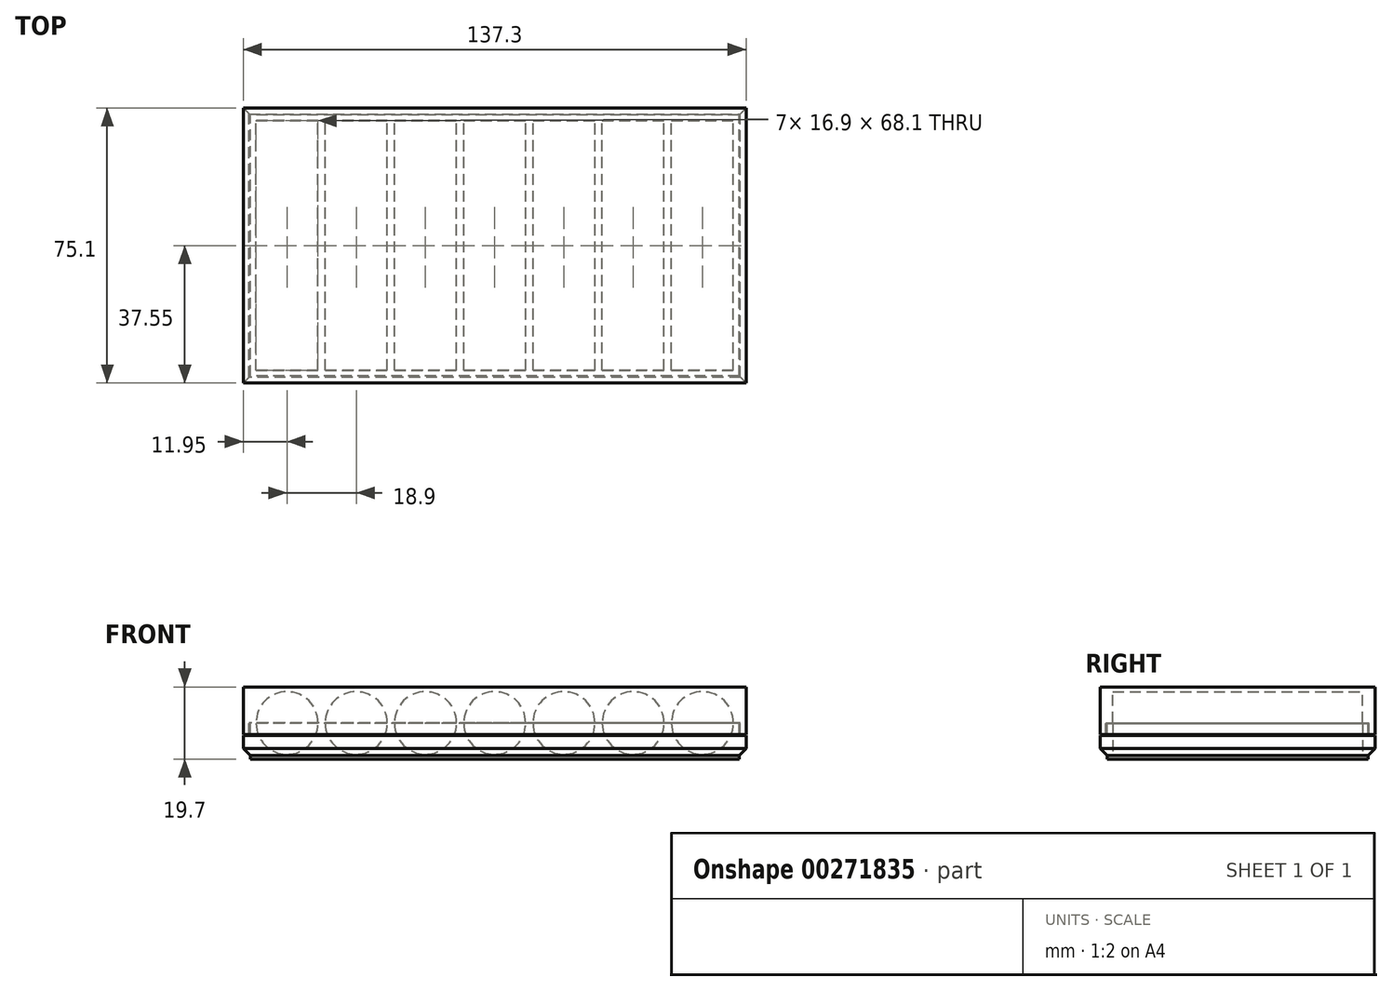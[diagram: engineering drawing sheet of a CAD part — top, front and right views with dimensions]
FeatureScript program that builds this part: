
annotation { "Feature Type Name" : "Feature", "Feature Type Description" : "" }
export const myFeature = defineFeature(function(context is Context, id is Id, definition is map)
    precondition{}
    {
        {
            assignVariable(context, id + "F0", {"name" : "chaff", "anyValue" : .3});
        }
        {
            assignVariable(context, id + "F1", {"name" : "basethick", "anyValue" : 1});
        }
        {
            assignVariable(context, id + "F2", {"name" : "diskdiam", "anyValue" : 16.3});
        }
        {
            assignVariable(context, id + "F3", {"name" : "lidrimdepth", "anyValue" : 3});
        }
        {
            var Q0;
            Q0=qCreatedBy(makeId("Top.planeOp"),FACE);
            var sketch = newSketch(context, id + "F4", { "sketchPlane" : qUnion([Q0])});
            skLineSegment(sketch, "E0.bottom", {"start": v(68.65, -37.55) * mm, "end": v(-68.65, -37.55) * mm});
            skLineSegment(sketch, "E0.top", {"start": v(68.65, 37.55) * mm, "end": v(-68.65, 37.55) * mm});
            skLineSegment(sketch, "E0.left", {"start": v(68.65, -37.55) * mm, "end": v(68.65, 37.55) * mm});
            skLineSegment(sketch, "E0.right", {"start": v(-68.65, -37.55) * mm, "end": v(-68.65, 37.55) * mm});
            skPoint(sketch, "E0.middle", {"position": v(0, 0) * mm});
            skSolve(sketch);
        }
        {
            var Q0;
            Q0=qSketchRegion(id+"F4",true);
            extrude(context, id + "F5", {"entities" : qUnion([Q0]), "depth" : (getVariable(context, 'basethick')) * mm});
        }
        {
            var Q0;
            Q0=makeQuery(id+"F5.opExtrude","CAP_FACE",FACE,{"disambiguationData":[OSD([sQuery(id+"F4.wireOp",EDGE,"E0.bottom"),sQuery(id+"F4.wireOp",EDGE,"E0.top"),sQuery(id+"F4.wireOp",EDGE,"E0.left"),sQuery(id+"F4.wireOp",EDGE,"E0.right")])],"isStart":false});
            var sketch = newSketch(context, id + "F6", { "sketchPlane" : qUnion([Q0])});
            skLineSegment(sketch, "E1.bottom", {"start": v(65.15, -34.05) * mm, "end": v(-65.15, -34.05) * mm});
            skLineSegment(sketch, "E1.top", {"start": v(65.15, 34.05) * mm, "end": v(-65.15, 34.05) * mm});
            skLineSegment(sketch, "E1.left", {"start": v(65.15, -34.05) * mm, "end": v(65.15, 34.05) * mm});
            skLineSegment(sketch, "E1.right", {"start": v(-65.15, -34.05) * mm, "end": v(-65.15, 34.05) * mm});
            skPoint(sketch, "E1.middle", {"position": v(0, 0) * mm});
            skLineSegment(sketch, "E2", {"start": v(-68.65, 0) * mm, "end": v(-65.15, 0) * mm, "construction": true});
            skLineSegment(sketch, "E3", {"start": v(0, 34.05) * mm, "end": v(0, 37.55) * mm, "construction": true});
            skLineSegment(sketch, "E4.0", {"start": v(-68.65, -37.55) * mm, "end": v(-68.65, 37.55) * mm});
            skLineSegment(sketch, "E5.0", {"start": v(68.65, -37.55) * mm, "end": v(-68.65, -37.55) * mm});
            skLineSegment(sketch, "E6.0", {"start": v(68.65, -37.55) * mm, "end": v(68.65, 37.55) * mm});
            skLineSegment(sketch, "E7.0", {"start": v(68.65, 37.55) * mm, "end": v(-68.65, 37.55) * mm});
            skSolve(sketch);
        }
        {
            var Q0;
            Q0=qSketchRegion(id+"F6",true);
            extrude(context, id + "F7", {"entities" : qUnion([Q0]), "operationType" : NewBodyOperationType.ADD, "depth" : (getVariable(context, 'diskdiam') / 2 + getVariable(context, 'chaff') * 2) * mm});
        }
        {
            var Q0;
            Q0=makeQuery(id+"F7.opExtrude","SWEPT_FACE",FACE,{"disambiguationData":[OSD([sQuery(id+"F6.wireOp",EDGE,"E1.top")])]});
            var sketch = newSketch(context, id + "F8", { "sketchPlane" : qUnion([Q0])});
            skLineSegment(sketch, "E8", {"start": v(-65.15, 9.75) * mm, "end": v(-48.25, 9.75) * mm});
            skArc(sketch, "E9", {"start": v(-65.15, 9.75) * mm, "mid": v(-56.7, 1.3) * mm, "end": v(-48.25, 9.75) * mm});
            skLineSegment(sketch, "E10.1.0.0", {"start": v(-46.25, 9.75) * mm, "end": v(-29.35, 9.75) * mm});
            skArc(sketch, "E10.1.0.1", {"start": v(-46.25, 9.75) * mm, "mid": v(-37.8, 1.3) * mm, "end": v(-29.35, 9.75) * mm});
            skLineSegment(sketch, "E10.2.0.0", {"start": v(-27.35, 9.75) * mm, "end": v(-10.45, 9.75) * mm});
            skArc(sketch, "E10.2.0.1", {"start": v(-27.35, 9.75) * mm, "mid": v(-18.9, 1.3) * mm, "end": v(-10.45, 9.75) * mm});
            skLineSegment(sketch, "E10.3.0.0", {"start": v(-8.45, 9.75) * mm, "end": v(8.45, 9.75) * mm});
            skArc(sketch, "E10.3.0.1", {"start": v(-8.45, 9.75) * mm, "mid": v(0, 1.3) * mm, "end": v(8.45, 9.75) * mm});
            skLineSegment(sketch, "E10.direction1", {"start": v(-65.15, 9.75) * mm, "end": v(-46.25, 9.75) * mm, "construction": true});
            skLineSegment(sketch, "E11.0", {"start": v(65.15, 1) * mm, "end": v(-65.15, 1) * mm});
            skLineSegment(sketch, "E12.0", {"start": v(-65.15, 9.75) * mm, "end": v(-65.15, 1) * mm});
            skLineSegment(sketch, "E13.0", {"start": v(65.15, 9.75) * mm, "end": v(65.15, 1) * mm});
            skLineSegment(sketch, "E14.0", {"start": v(65.15, 9.75) * mm, "end": v(-65.15, 9.75) * mm});
            skLineSegment(sketch, "E15.0.4.0", {"start": v(10.45, 9.75) * mm, "end": v(27.35, 9.75) * mm});
            skArc(sketch, "E15.3.4.0", {"start": v(10.45, 9.75) * mm, "mid": v(18.9, 1.3) * mm, "end": v(27.35, 9.75) * mm});
            skLineSegment(sketch, "E15.0.5.0", {"start": v(29.35, 9.75) * mm, "end": v(46.25, 9.75) * mm});
            skArc(sketch, "E15.3.5.0", {"start": v(29.35, 9.75) * mm, "mid": v(37.8, 1.3) * mm, "end": v(46.25, 9.75) * mm});
            skLineSegment(sketch, "E15.0.6.0", {"start": v(48.25, 9.75) * mm, "end": v(65.15, 9.75) * mm});
            skArc(sketch, "E15.3.6.0", {"start": v(48.25, 9.75) * mm, "mid": v(56.7, 1.3) * mm, "end": v(65.15, 9.75) * mm});
            skSolve(sketch);
        }
        {
            var Q0;
            {var subQ5=sQuery(id+"F8.wireOp",EDGE,"E9");Q0=makeQuery(id+"F8.imprint","IMPRINT",FACE,{"disambiguationData":[TD([[makeQuery(id+"F8.imprint","IMPRINT",EDGE,{"derivedFrom":subQ5}),-1.0]])]});}
            var Q1;
            Q1=makeQuery(id+"F7.opExtrude","SWEPT_FACE",FACE,{"disambiguationData":[OSD([sQuery(id+"F6.wireOp",EDGE,"E1.bottom")])]});
            extrude(context, id + "F9", {"entities" : qUnion([Q0]), "operationType" : NewBodyOperationType.ADD, "endBound" : BoundingType.UP_TO_SURFACE, "endBoundEntityFace" : qUnion([Q1]), "depth" : 25 * mm});
        }
        {
            var Q0;
            {var subQ0=sQuery(id+"F8.wireOp",EDGE,"E14.0");var subQ1=sQuery(id+"F8.wireOp",EDGE,"E10.1.0.1");var subQ2=sQuery(id+"F8.wireOp",EDGE,"E10.2.0.1");Q0=makeQuery(id+"F9.boolean.opBoolean","MERGE",FACE,{"derivedFrom":[makeQuery(id+"F7.opExtrude","CAP_FACE",FACE,{"disambiguationData":[OSD([sQuery(id+"F6.wireOp",EDGE,"E1.bottom"),sQuery(id+"F6.wireOp",EDGE,"E1.top"),sQuery(id+"F6.wireOp",EDGE,"E1.left"),sQuery(id+"F6.wireOp",EDGE,"E1.right"),sQuery(id+"F6.wireOp",EDGE,"E4.0"),sQuery(id+"F6.wireOp",EDGE,"E5.0"),sQuery(id+"F6.wireOp",EDGE,"E6.0"),sQuery(id+"F6.wireOp",EDGE,"E7.0")])],"isStart":false}),makeQuery(id+"F9.opExtrude","SWEPT_FACE",FACE,{"disambiguationData":[OSD([subQ0]),TDD([makeQuery(id+"F8.imprint","IMPRINT",EDGE,{"disambiguationData":[TD([[makeQuery(id+"F8.imprint","INTERSECT",VERTEX,{"derivedFrom":[sQuery(id+"F8.wireOp",EDGE,"E13.0"),subQ0]}),-1.0]])],"derivedFrom":subQ0})])]}),makeQuery(id+"F9.opExtrude","SWEPT_FACE",FACE,{"disambiguationData":[OSD([subQ0]),TDD([makeQuery(id+"F8.imprint","IMPRINT",EDGE,{"disambiguationData":[TD([[makeQuery(id+"F8.imprint","INTERSECT",VERTEX,{"disambiguationData":[OD(1.0)],"derivedFrom":[subQ2,subQ0]}),1.0]])],"derivedFrom":subQ0})])]}),makeQuery(id+"F9.opExtrude","SWEPT_FACE",FACE,{"disambiguationData":[OSD([subQ0]),TDD([makeQuery(id+"F8.imprint","IMPRINT",EDGE,{"disambiguationData":[TD([[makeQuery(id+"F8.imprint","INTERSECT",VERTEX,{"disambiguationData":[OD(1.0)],"derivedFrom":[subQ1,subQ0]}),1.0]])],"derivedFrom":subQ0})])]}),makeQuery(id+"F9.opExtrude","SWEPT_FACE",FACE,{"disambiguationData":[OSD([subQ0]),TDD([makeQuery(id+"F8.imprint","IMPRINT",EDGE,{"disambiguationData":[TD([[makeQuery(id+"F8.imprint","INTERSECT",VERTEX,{"derivedFrom":[sQuery(id+"F8.wireOp",EDGE,"E9"),subQ0]}),1.0]])],"derivedFrom":subQ0})])]})]});}
            cPlane(context, id + "F10", {"entities" : qUnion([Q0]), "cplaneType" : CPlaneType.OFFSET, "offset" : .1 * mm, "width" : 150 * mm, "height" : 150 * mm});
        }
        {
            var Q0;
            Q0=makeQuery(id+"F5.opExtrude","SWEPT_BODY",BODY,{"disambiguationData":[OSD([sQuery(id+"F4.wireOp",EDGE,"E0.bottom"),sQuery(id+"F4.wireOp",EDGE,"E0.top"),sQuery(id+"F4.wireOp",EDGE,"E0.left"),sQuery(id+"F4.wireOp",EDGE,"E0.right")])]});
            var Q1;
            Q1=qCreatedBy(id+"F10.planeOp",FACE);
            mirror(context, id + "F11", {"entities" : qUnion([Q0]), "mirrorPlane" : qUnion([Q1])});
        }
        {
            var Q0;
            {var subQ0=sQuery(id+"F8.wireOp",EDGE,"E14.0");var subQ1=sQuery(id+"F8.wireOp",EDGE,"E10.1.0.1");var subQ2=sQuery(id+"F8.wireOp",EDGE,"E10.2.0.1");Q0=makeQuery(id+"F9.boolean.opBoolean","MERGE",FACE,{"derivedFrom":[makeQuery(id+"F7.opExtrude","CAP_FACE",FACE,{"disambiguationData":[OSD([sQuery(id+"F6.wireOp",EDGE,"E1.bottom"),sQuery(id+"F6.wireOp",EDGE,"E1.top"),sQuery(id+"F6.wireOp",EDGE,"E1.left"),sQuery(id+"F6.wireOp",EDGE,"E1.right"),sQuery(id+"F6.wireOp",EDGE,"E4.0"),sQuery(id+"F6.wireOp",EDGE,"E5.0"),sQuery(id+"F6.wireOp",EDGE,"E6.0"),sQuery(id+"F6.wireOp",EDGE,"E7.0")])],"isStart":false}),makeQuery(id+"F9.opExtrude","SWEPT_FACE",FACE,{"disambiguationData":[OSD([subQ0]),TDD([makeQuery(id+"F8.imprint","IMPRINT",EDGE,{"disambiguationData":[TD([[makeQuery(id+"F8.imprint","INTERSECT",VERTEX,{"derivedFrom":[sQuery(id+"F8.wireOp",EDGE,"E13.0"),subQ0]}),-1.0]])],"derivedFrom":subQ0})])]}),makeQuery(id+"F9.opExtrude","SWEPT_FACE",FACE,{"disambiguationData":[OSD([subQ0]),TDD([makeQuery(id+"F8.imprint","IMPRINT",EDGE,{"disambiguationData":[TD([[makeQuery(id+"F8.imprint","INTERSECT",VERTEX,{"disambiguationData":[OD(1.0)],"derivedFrom":[subQ2,subQ0]}),1.0]])],"derivedFrom":subQ0})])]}),makeQuery(id+"F9.opExtrude","SWEPT_FACE",FACE,{"disambiguationData":[OSD([subQ0]),TDD([makeQuery(id+"F8.imprint","IMPRINT",EDGE,{"disambiguationData":[TD([[makeQuery(id+"F8.imprint","INTERSECT",VERTEX,{"disambiguationData":[OD(1.0)],"derivedFrom":[subQ1,subQ0]}),1.0]])],"derivedFrom":subQ0})])]}),makeQuery(id+"F9.opExtrude","SWEPT_FACE",FACE,{"disambiguationData":[OSD([subQ0]),TDD([makeQuery(id+"F8.imprint","IMPRINT",EDGE,{"disambiguationData":[TD([[makeQuery(id+"F8.imprint","INTERSECT",VERTEX,{"derivedFrom":[sQuery(id+"F8.wireOp",EDGE,"E9"),subQ0]}),1.0]])],"derivedFrom":subQ0})])]})]});}
            var sketch = newSketch(context, id + "F12", { "sketchPlane" : qUnion([Q0])});
            skLineSegment(sketch, "E16.0", {"start": v(68.65, 37.55) * mm, "end": v(-68.65, 37.55) * mm});
            skLineSegment(sketch, "E17.0", {"start": v(-68.65, -37.55) * mm, "end": v(-68.65, 37.55) * mm});
            skLineSegment(sketch, "E18.0", {"start": v(68.65, -37.55) * mm, "end": v(-68.65, -37.55) * mm});
            skLineSegment(sketch, "E19.0", {"start": v(68.65, -37.55) * mm, "end": v(68.65, 37.55) * mm});
            skLineSegment(sketch, "E20.0", {"start": v(66.75, 35.65) * mm, "end": v(-66.75, 35.65) * mm});
            skLineSegment(sketch, "E20.1", {"start": v(66.75, -35.65) * mm, "end": v(66.75, 35.65) * mm});
            skLineSegment(sketch, "E20.2", {"start": v(66.75, -35.65) * mm, "end": v(-66.75, -35.65) * mm});
            skLineSegment(sketch, "E20.3", {"start": v(-66.75, -35.65) * mm, "end": v(-66.75, 35.65) * mm});
            skSolve(sketch);
        }
        {
            var Q0;
            Q0=makeQuery(id+"F12.imprint","IMPRINT",FACE,{"disambiguationData":[TD([[makeQuery(id+"F12.imprint","IMPRINT",EDGE,{"derivedFrom":sQuery(id+"F12.wireOp",EDGE,"E16.0")}),1.0]])]});
            extrude(context, id + "F13", {"entities" : qUnion([Q0]), "operationType" : NewBodyOperationType.REMOVE, "oppositeDirection" : true, "depth" : (getVariable(context, 'lidrimdepth') + getVariable(context, 'chaff')) * mm});
        }
        {
            var Q0;
            Q0=makeQuery(id+"F5.opExtrude","CAP_FACE",FACE,{"disambiguationData":[OSD([sQuery(id+"F4.wireOp",EDGE,"E0.bottom"),sQuery(id+"F4.wireOp",EDGE,"E0.top"),sQuery(id+"F4.wireOp",EDGE,"E0.left"),sQuery(id+"F4.wireOp",EDGE,"E0.right")])],"isStart":true});
            var sketch = newSketch(context, id + "F14", { "sketchPlane" : qUnion([Q0])});
            skLineSegment(sketch, "E21.0", {"start": v(68.65, 37.55) * mm, "end": v(-68.65, 37.55) * mm});
            skLineSegment(sketch, "E22.0", {"start": v(-68.65, 37.55) * mm, "end": v(-68.65, -37.55) * mm});
            skLineSegment(sketch, "E23.0", {"start": v(68.65, 37.55) * mm, "end": v(68.65, -37.55) * mm});
            skLineSegment(sketch, "E24.0", {"start": v(68.65, -37.55) * mm, "end": v(-68.65, -37.55) * mm});
            skLineSegment(sketch, "E25.0", {"start": v(66.75, 35.65) * mm, "end": v(-66.75, 35.65) * mm});
            skLineSegment(sketch, "E25.1", {"start": v(66.75, 35.65) * mm, "end": v(66.75, -35.65) * mm});
            skLineSegment(sketch, "E25.2", {"start": v(66.75, -35.65) * mm, "end": v(-66.75, -35.65) * mm});
            skLineSegment(sketch, "E25.3", {"start": v(-66.75, 35.65) * mm, "end": v(-66.75, -35.65) * mm});
            skSolve(sketch);
        }
        {
            var Q0;
            Q0=qSketchRegion(id+"F14",true);
            extrude(context, id + "F15", {"entities" : qUnion([Q0]), "operationType" : NewBodyOperationType.REMOVE, "oppositeDirection" : true, "depth" : (getVariable(context, 'lidrimdepth')) * mm});
        }
        {
            var Q0;
            Q0=makeQuery(id+"F15.boolean.opBoolean","COPY",EDGE,{"derivedFrom":makeQuery(id+"F15.opExtrude","CAP_EDGE",EDGE,{"disambiguationData":[OSD([sQuery(id+"F14.wireOp",EDGE,"E25.0")])],"isStart":false})});
            var Q1;
            Q1=makeQuery(id+"F15.boolean.opBoolean","COPY",EDGE,{"derivedFrom":makeQuery(id+"F15.opExtrude","CAP_EDGE",EDGE,{"disambiguationData":[OSD([sQuery(id+"F14.wireOp",EDGE,"E25.3")])],"isStart":false})});
            var Q2;
            Q2=makeQuery(id+"F15.boolean.opBoolean","COPY",EDGE,{"derivedFrom":makeQuery(id+"F15.opExtrude","CAP_EDGE",EDGE,{"disambiguationData":[OSD([sQuery(id+"F14.wireOp",EDGE,"E25.2")])],"isStart":false})});
            var Q3;
            Q3=makeQuery(id+"F15.boolean.opBoolean","COPY",EDGE,{"derivedFrom":makeQuery(id+"F15.opExtrude","CAP_EDGE",EDGE,{"disambiguationData":[OSD([sQuery(id+"F14.wireOp",EDGE,"E25.1")])],"isStart":false})});
            chamfer(context, id + "F16", {"entities" : qUnion([Q0, Q1, Q2, Q3]), "width" : 2 * mm, "tangentPropagation" : true});
        }
        {
            var Q0;
            {var subQ0=sQuery(id+"F8.wireOp",EDGE,"E14.0");var subQ1=sQuery(id+"F8.wireOp",EDGE,"E10.1.0.1");var subQ2=sQuery(id+"F8.wireOp",EDGE,"E10.2.0.1");Q0=makeQuery(id+"F11.opPattern","COPY",FACE,{"derivedFrom":makeQuery(id+"F9.boolean.opBoolean","MERGE",FACE,{"derivedFrom":[makeQuery(id+"F7.opExtrude","CAP_FACE",FACE,{"disambiguationData":[OSD([sQuery(id+"F6.wireOp",EDGE,"E1.bottom"),sQuery(id+"F6.wireOp",EDGE,"E1.top"),sQuery(id+"F6.wireOp",EDGE,"E1.left"),sQuery(id+"F6.wireOp",EDGE,"E1.right"),sQuery(id+"F6.wireOp",EDGE,"E4.0"),sQuery(id+"F6.wireOp",EDGE,"E5.0"),sQuery(id+"F6.wireOp",EDGE,"E6.0"),sQuery(id+"F6.wireOp",EDGE,"E7.0")])],"isStart":false}),makeQuery(id+"F9.opExtrude","SWEPT_FACE",FACE,{"disambiguationData":[OSD([subQ0]),TDD([makeQuery(id+"F8.imprint","IMPRINT",EDGE,{"disambiguationData":[TD([[makeQuery(id+"F8.imprint","INTERSECT",VERTEX,{"derivedFrom":[sQuery(id+"F8.wireOp",EDGE,"E13.0"),subQ0]}),-1.0]])],"derivedFrom":subQ0})])]}),makeQuery(id+"F9.opExtrude","SWEPT_FACE",FACE,{"disambiguationData":[OSD([subQ0]),TDD([makeQuery(id+"F8.imprint","IMPRINT",EDGE,{"disambiguationData":[TD([[makeQuery(id+"F8.imprint","INTERSECT",VERTEX,{"disambiguationData":[OD(1.0)],"derivedFrom":[subQ2,subQ0]}),1.0]])],"derivedFrom":subQ0})])]}),makeQuery(id+"F9.opExtrude","SWEPT_FACE",FACE,{"disambiguationData":[OSD([subQ0]),TDD([makeQuery(id+"F8.imprint","IMPRINT",EDGE,{"disambiguationData":[TD([[makeQuery(id+"F8.imprint","INTERSECT",VERTEX,{"disambiguationData":[OD(1.0)],"derivedFrom":[subQ1,subQ0]}),1.0]])],"derivedFrom":subQ0})])]}),makeQuery(id+"F9.opExtrude","SWEPT_FACE",FACE,{"disambiguationData":[OSD([subQ0]),TDD([makeQuery(id+"F8.imprint","IMPRINT",EDGE,{"disambiguationData":[TD([[makeQuery(id+"F8.imprint","INTERSECT",VERTEX,{"derivedFrom":[sQuery(id+"F8.wireOp",EDGE,"E9"),subQ0]}),1.0]])],"derivedFrom":subQ0})])]})]}),"instanceName":"1"});}
            var sketch = newSketch(context, id + "F17", { "sketchPlane" : qUnion([Q0])});
            skPoint(sketch, "E26.0", {"position": v(-65.15, 34.05) * mm});
            skPoint(sketch, "E27.0", {"position": v(-65.15, -34.05) * mm});
            skLineSegment(sketch, "E28", {"start": v(-65.15, 34.05) * mm, "end": v(-65.15, -34.05) * mm, "construction": true});
            skLineSegment(sketch, "E29.0", {"start": v(67.05, 35.95) * mm, "end": v(-67.05, 35.95) * mm});
            skLineSegment(sketch, "E29.1", {"start": v(67.05, 35.95) * mm, "end": v(67.05, -35.95) * mm});
            skLineSegment(sketch, "E29.2", {"start": v(-67.05, -35.95) * mm, "end": v(67.05, -35.95) * mm});
            skLineSegment(sketch, "E29.3", {"start": v(-67.05, 35.95) * mm, "end": v(-67.05, -35.95) * mm});
            skLineSegment(sketch, "E30.0", {"start": v(68.65, 37.55) * mm, "end": v(-68.65, 37.55) * mm});
            skLineSegment(sketch, "E31.0", {"start": v(68.65, 37.55) * mm, "end": v(68.65, -37.55) * mm});
            skLineSegment(sketch, "E32.0", {"start": v(68.65, -37.55) * mm, "end": v(-68.65, -37.55) * mm});
            skLineSegment(sketch, "E33.0", {"start": v(-68.65, 37.55) * mm, "end": v(-68.65, -37.55) * mm});
            skPoint(sketch, "E34", {"position": v(65.15, 34.05) * mm});
            skPoint(sketch, "E35", {"position": v(65.15, -34.05) * mm});
            skLineSegment(sketch, "E36", {"start": v(-65.15, 34.05) * mm, "end": v(65.15, 34.05) * mm, "construction": true});
            skLineSegment(sketch, "E37", {"start": v(-65.15, -34.05) * mm, "end": v(65.15, -34.05) * mm, "construction": true});
            skLineSegment(sketch, "E38", {"start": v(0, 35.95) * mm, "end": v(0, 34.05) * mm, "construction": true});
            skLineSegment(sketch, "E39", {"start": v(-67.05, 0) * mm, "end": v(-65.15, 0) * mm, "construction": true});
            skSolve(sketch);
        }
        {
            var Q0;
            Q0=qSketchRegion(id+"F17",true);
            extrude(context, id + "F18", {"entities" : qUnion([Q0]), "operationType" : NewBodyOperationType.ADD, "depth" : 3.2 * mm});
        }
    });
